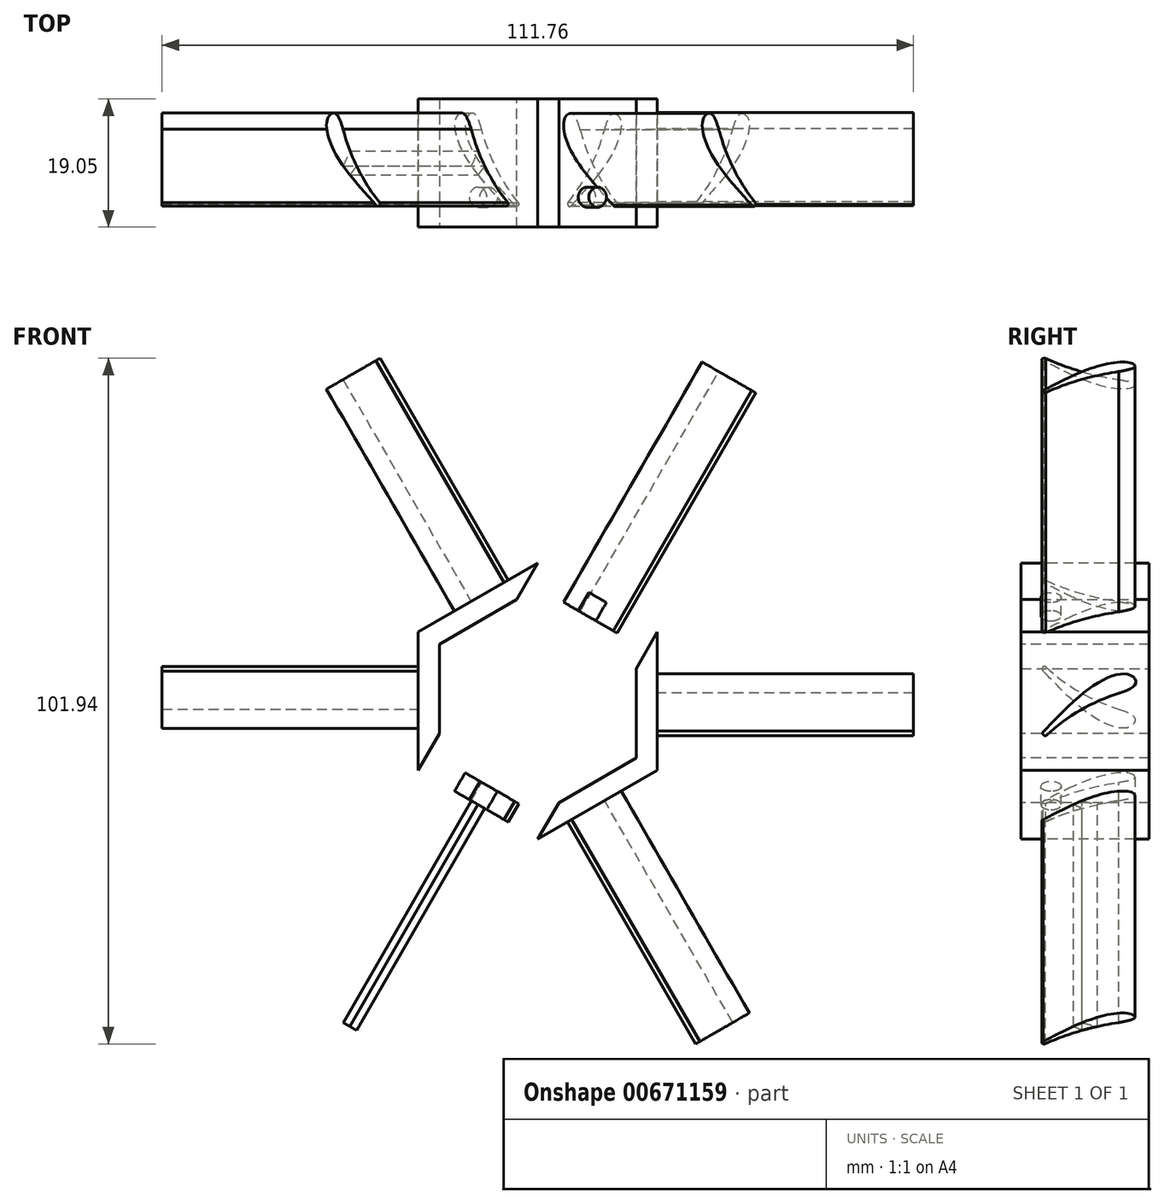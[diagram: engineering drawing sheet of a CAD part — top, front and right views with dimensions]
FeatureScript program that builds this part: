
annotation { "Feature Type Name" : "Feature", "Feature Type Description" : "" }
export const myFeature = defineFeature(function(context is Context, id is Id, definition is map)
    precondition{}
    {
        {
            var Q0;
            Q0=qCreatedBy(makeId("Front.planeOp"),FACE);
            var sketch = newSketch(context, id + "F0", { "sketchPlane" : qUnion([Q0])});
            skCircle(sketch, "E0.cCircle", {"center": v(0, 0) * mm, "radius": 17.78 * mm, "construction": true});
            skLineSegment(sketch, "E0.0", {"start": v(17.78, 10.27) * mm, "end": v(17.78, -10.27) * mm});
            skLineSegment(sketch, "E0.1", {"start": v(17.78, -10.27) * mm, "end": v(0, -20.53) * mm});
            skLineSegment(sketch, "E0.2", {"start": v(0, -20.53) * mm, "end": v(-17.78, -10.27) * mm});
            skLineSegment(sketch, "E0.3", {"start": v(-17.78, -10.27) * mm, "end": v(-17.78, 10.27) * mm});
            skLineSegment(sketch, "E0.4", {"start": v(-17.78, 10.27) * mm, "end": v(0, 20.53) * mm});
            skLineSegment(sketch, "E0.5", {"start": v(0, 20.53) * mm, "end": v(17.78, 10.27) * mm});
            skPoint(sketch, "E0.0.midPoint", {"position": v(17.78, 0) * mm});
            skSolve(sketch);
        }
        {
            var Q0;
            Q0=makeQuery(id+"F0.imprint","IMPRINT",FACE,{"disambiguationData":[TD([[makeQuery(id+"F0.imprint","IMPRINT",EDGE,{"derivedFrom":sQuery(id+"F0.wireOp",EDGE,"E0.0")}),-1.0]])]});
            extrude(context, id + "F1", {"entities" : qUnion([Q0]), "depth" : 19.05 * mm, "offsetDistance" : 25.4 * mm});
        }
        {
            var Q0;
            Q0=makeQuery(id+"F1.opExtrude","SWEPT_FACE",FACE,{"disambiguationData":[OSD([sQuery(id+"F0.wireOp",EDGE,"E0.5")])]});
            var sketch = newSketch(context, id + "F2", { "sketchPlane" : qUnion([Q0])});
            skLineSegment(sketch, "E1", {"start": v(0, 0) * mm, "end": v(0, -19.05) * mm});
            skPoint(sketch, "E2", {"position": v(0, -9.53) * mm});
            skFitSpline(sketch, "E3", {"points": [v(-1.19, -14.5) * mm, v(-2.57, -16.9) * mm, v(-3.83, -16.16) * mm, v(-2.94, -11.66) * mm, v(4.47, -3.26) * mm], "startDerivative": vector(-5.87, -16.48) * mm, "endDerivative": vector(22.04, 21.13) * mm});
            skArc(sketch, "E4", {"start": v(5.1, -3.62) * mm, "mid": v(1.33, -8.7) * mm, "end": v(-1.19, -14.5) * mm});
            skArc(sketch, "E5", {"start": v(5.1, -3.62) * mm, "mid": v(4.97, -3.12) * mm, "end": v(4.47, -3.26) * mm});
            skLineSegment(sketch, "E6", {"start": v(0, 0) * mm, "end": v(0, -4.45) * mm});
            skCircle(sketch, "E7", {"center": v(0, -4.45) * mm, "radius": 1.5 * mm});
            skSolve(sketch);
        }
        {
            var Q0;
            Q0=makeQuery(id+"F1.opExtrude","SWEPT_FACE",FACE,{"disambiguationData":[OSD([sQuery(id+"F0.wireOp",EDGE,"E0.0")])]});
            var sketch = newSketch(context, id + "F3", { "sketchPlane" : qUnion([Q0])});
            skLineSegment(sketch, "E8", {"start": v(0, 0) * mm, "end": v(-19.05, 0) * mm});
            skLineSegment(sketch, "E9", {"start": v(0.25, 0) * mm, "end": v(-18.8, 0) * mm});
            skFitSpline(sketch, "E10", {"points": [v(-14.64, 1.2) * mm, v(-17.02, 2.57) * mm, v(-16.3, 3.84) * mm, v(-11.79, 2.95) * mm, v(-3.39, -4.47) * mm], "startDerivative": vector(-16.48, 5.87) * mm, "endDerivative": vector(21.13, -22.04) * mm});
            skArc(sketch, "E11", {"start": v(-3.75, -5.1) * mm, "mid": v(-8.83, -1.33) * mm, "end": v(-14.64, 1.2) * mm});
            skArc(sketch, "E12", {"start": v(-3.75, -5.1) * mm, "mid": v(-3.25, -4.97) * mm, "end": v(-3.39, -4.47) * mm});
            skLineSegment(sketch, "E13", {"start": v(0, 0) * mm, "end": v(-4.44, 0) * mm});
            skCircle(sketch, "E14", {"center": v(-4.44, 0) * mm, "radius": 1.5 * mm});
            skSolve(sketch);
        }
        {
            var Q0;
            Q0=makeQuery(id+"F1.opExtrude","SWEPT_FACE",FACE,{"disambiguationData":[OSD([sQuery(id+"F0.wireOp",EDGE,"E0.1")])]});
            var sketch = newSketch(context, id + "F4", { "sketchPlane" : qUnion([Q0])});
            skLineSegment(sketch, "E15", {"start": v(0, 0) * mm, "end": v(0, 19.05) * mm});
            skLineSegment(sketch, "E16", {"start": v(0, 0) * mm, "end": v(0, 19.04) * mm});
            skFitSpline(sketch, "E17", {"points": [v(1.2, 14.5) * mm, v(2.57, 16.88) * mm, v(3.84, 16.15) * mm, v(2.95, 11.65) * mm, v(-4.46, 3.25) * mm], "startDerivative": vector(5.87, 16.48) * mm, "endDerivative": vector(-22.04, -21.13) * mm});
            skArc(sketch, "E18", {"start": v(-5.1, 3.61) * mm, "mid": v(-1.33, 8.7) * mm, "end": v(1.2, 14.5) * mm});
            skArc(sketch, "E19", {"start": v(-5.1, 3.61) * mm, "mid": v(-4.97, 3.11) * mm, "end": v(-4.46, 3.25) * mm});
            skLineSegment(sketch, "E20", {"start": v(0, 0) * mm, "end": v(0, 4.44) * mm});
            skCircle(sketch, "E21", {"center": v(0, 4.44) * mm, "radius": 1.5 * mm});
            skSolve(sketch);
        }
        {
            var Q0;
            Q0=makeQuery(id+"F1.opExtrude","SWEPT_FACE",FACE,{"disambiguationData":[OSD([sQuery(id+"F0.wireOp",EDGE,"E0.2")])]});
            var sketch = newSketch(context, id + "F5", { "sketchPlane" : qUnion([Q0])});
            skLineSegment(sketch, "E22", {"start": v(0, 0) * mm, "end": v(0, 19.05) * mm});
            skLineSegment(sketch, "E23", {"start": v(0, 0.04) * mm, "end": v(0, 19.09) * mm});
            skFitSpline(sketch, "E24", {"points": [v(1.18, 14.54) * mm, v(2.56, 16.93) * mm, v(3.83, 16.2) * mm, v(2.94, 11.7) * mm, v(-4.47, 3.3) * mm], "startDerivative": vector(5.87, 16.48) * mm, "endDerivative": vector(-22.04, -21.13) * mm});
            skArc(sketch, "E25", {"start": v(-5.11, 3.66) * mm, "mid": v(-1.34, 8.74) * mm, "end": v(1.18, 14.54) * mm});
            skArc(sketch, "E26", {"start": v(-5.11, 3.66) * mm, "mid": v(-4.98, 3.16) * mm, "end": v(-4.47, 3.3) * mm});
            skSolve(sketch);
        }
        {
            var Q0;
            Q0=makeQuery(id+"F1.opExtrude","SWEPT_FACE",FACE,{"disambiguationData":[OSD([sQuery(id+"F0.wireOp",EDGE,"E0.3")])]});
            var sketch = newSketch(context, id + "F6", { "sketchPlane" : qUnion([Q0])});
            skLineSegment(sketch, "E27", {"start": v(0, 0) * mm, "end": v(19.05, 0) * mm});
            skLineSegment(sketch, "E28", {"start": v(0.03, 0) * mm, "end": v(19.08, 0) * mm});
            skFitSpline(sketch, "E29", {"points": [v(14.53, -1.19) * mm, v(16.92, -2.57) * mm, v(16.19, -3.83) * mm, v(11.68, -2.94) * mm, v(3.28, 4.47) * mm], "startDerivative": vector(16.48, -5.87) * mm, "endDerivative": vector(-21.13, 22.04) * mm});
            skArc(sketch, "E30", {"start": v(3.65, 5.1) * mm, "mid": v(8.73, 1.33) * mm, "end": v(14.53, -1.19) * mm});
            skArc(sketch, "E31", {"start": v(3.65, 5.1) * mm, "mid": v(3.15, 4.97) * mm, "end": v(3.28, 4.47) * mm});
            skSolve(sketch);
        }
        {
            var Q0;
            Q0=makeQuery(id+"F1.opExtrude","SWEPT_FACE",FACE,{"disambiguationData":[OSD([sQuery(id+"F0.wireOp",EDGE,"E0.4")])]});
            var sketch = newSketch(context, id + "F7", { "sketchPlane" : qUnion([Q0])});
            skLineSegment(sketch, "E32", {"start": v(0, 0) * mm, "end": v(0, -19.05) * mm});
            skLineSegment(sketch, "E33", {"start": v(0, -0.02) * mm, "end": v(0, -19.07) * mm});
            skFitSpline(sketch, "E34", {"points": [v(-1.19, -14.52) * mm, v(-2.57, -16.91) * mm, v(-3.83, -16.18) * mm, v(-2.94, -11.68) * mm, v(4.47, -3.28) * mm], "startDerivative": vector(-5.87, -16.48) * mm, "endDerivative": vector(22.04, 21.13) * mm});
            skArc(sketch, "E35", {"start": v(5.1, -3.64) * mm, "mid": v(1.33, -8.72) * mm, "end": v(-1.19, -14.52) * mm});
            skArc(sketch, "E36", {"start": v(5.1, -3.64) * mm, "mid": v(4.97, -3.14) * mm, "end": v(4.47, -3.28) * mm});
            skSolve(sketch);
        }
        {
            var Q0;
            {var subQ0=sQuery(id+"F7.wireOp",EDGE,"E34");var subQ1=sQuery(id+"F7.wireOp",EDGE,"E32");var subQ2=makeQuery(id+"F7.imprint","INTERSECT",VERTEX,{"derivedFrom":[subQ1,subQ0]});Q0=makeQuery(id+"F7.imprint","IMPRINT",FACE,{"disambiguationData":[TD([[makeQuery(id+"F7.imprint","IMPRINT",EDGE,{"disambiguationData":[TD([[subQ2,-1.0]])],"derivedFrom":subQ1}),-1.0]])]});}
            var Q1;
            {var subQ5=sQuery(id+"F7.wireOp",EDGE,"E36");Q1=makeQuery(id+"F7.imprint","IMPRINT",FACE,{"disambiguationData":[TD([[makeQuery(id+"F7.imprint","IMPRINT",EDGE,{"derivedFrom":subQ5}),1.0]])]});}
            extrude(context, id + "F8", {"entities" : qUnion([Q0, Q1]), "operationType" : NewBodyOperationType.ADD, "depth" : 38.1 * mm, "offsetDistance" : 25.4 * mm});
        }
        {
            var Q0;
            {var subQ0=sQuery(id+"F2.wireOp",EDGE,"E3");var subQ1=sQuery(id+"F2.wireOp",EDGE,"E1");var subQ2=makeQuery(id+"F2.imprint","INTERSECT",VERTEX,{"derivedFrom":[subQ1,subQ0]});Q0=makeQuery(id+"F2.imprint","IMPRINT",FACE,{"disambiguationData":[TD([[makeQuery(id+"F2.imprint","IMPRINT",EDGE,{"disambiguationData":[TD([[subQ2,-1.0]])],"derivedFrom":subQ1}),-1.0]])]});}
            var Q1;
            {var subQ5=sQuery(id+"F2.wireOp",EDGE,"E5");Q1=makeQuery(id+"F2.imprint","IMPRINT",FACE,{"disambiguationData":[TD([[makeQuery(id+"F2.imprint","IMPRINT",EDGE,{"derivedFrom":subQ5}),1.0]])]});}
            extrude(context, id + "F9", {"entities" : qUnion([Q0, Q1]), "operationType" : NewBodyOperationType.ADD, "depth" : 38.1 * mm, "offsetDistance" : 25.4 * mm});
        }
        {
            var Q0;
            {var subQ0=sQuery(id+"F3.wireOp",EDGE,"E10");var subQ1=sQuery(id+"F3.wireOp",EDGE,"E9");var subQ2=makeQuery(id+"F3.imprint","INTERSECT",VERTEX,{"derivedFrom":[subQ1,subQ0]});Q0=makeQuery(id+"F3.imprint","IMPRINT",FACE,{"disambiguationData":[TD([[makeQuery(id+"F3.imprint","IMPRINT",EDGE,{"disambiguationData":[TD([[subQ2,-1.0]])],"derivedFrom":subQ1}),-1.0]])]});}
            var Q1;
            {var subQ5=sQuery(id+"F3.wireOp",EDGE,"E12");Q1=makeQuery(id+"F3.imprint","IMPRINT",FACE,{"disambiguationData":[TD([[makeQuery(id+"F3.imprint","IMPRINT",EDGE,{"derivedFrom":subQ5}),1.0]])]});}
            extrude(context, id + "F10", {"entities" : qUnion([Q0, Q1]), "operationType" : NewBodyOperationType.ADD, "depth" : 38.1 * mm, "offsetDistance" : 25.4 * mm});
        }
        {
            var Q0;
            {var subQ0=sQuery(id+"F4.wireOp",EDGE,"E18");var subQ1=sQuery(id+"F4.wireOp",EDGE,"E16");var subQ2=makeQuery(id+"F4.imprint","INTERSECT",VERTEX,{"derivedFrom":[subQ1,subQ0]});Q0=makeQuery(id+"F4.imprint","IMPRINT",FACE,{"disambiguationData":[TD([[makeQuery(id+"F4.imprint","IMPRINT",EDGE,{"disambiguationData":[TD([[subQ2,1.0]])],"derivedFrom":subQ1}),-1.0]])]});}
            var Q1;
            {var subQ5=sQuery(id+"F4.wireOp",EDGE,"E19");Q1=makeQuery(id+"F4.imprint","IMPRINT",FACE,{"disambiguationData":[TD([[makeQuery(id+"F4.imprint","IMPRINT",EDGE,{"derivedFrom":subQ5}),1.0]])]});}
            extrude(context, id + "F11", {"entities" : qUnion([Q0, Q1]), "operationType" : NewBodyOperationType.ADD, "depth" : 38.1 * mm, "offsetDistance" : 25.4 * mm});
        }
        {
            var Q0;
            {var subQ0=sQuery(id+"F5.wireOp",EDGE,"E24");var subQ1=sQuery(id+"F5.wireOp",EDGE,"E22");var subQ2=makeQuery(id+"F5.imprint","INTERSECT",VERTEX,{"derivedFrom":[subQ1,subQ0]});Q0=makeQuery(id+"F5.imprint","IMPRINT",FACE,{"disambiguationData":[TD([[makeQuery(id+"F5.imprint","IMPRINT",EDGE,{"disambiguationData":[TD([[subQ2,-1.0]])],"derivedFrom":subQ1}),-1.0]])]});}
            var Q1;
            {var subQ5=sQuery(id+"F5.wireOp",EDGE,"E26");Q1=makeQuery(id+"F5.imprint","IMPRINT",FACE,{"disambiguationData":[TD([[makeQuery(id+"F5.imprint","IMPRINT",EDGE,{"derivedFrom":subQ5}),1.0]])]});}
            extrude(context, id + "F12", {"entities" : qUnion([Q0, Q1]), "operationType" : NewBodyOperationType.ADD, "depth" : 38.1 * mm, "offsetDistance" : 25.4 * mm});
        }
        {
            var Q0;
            {var subQ0=sQuery(id+"F6.wireOp",EDGE,"E29");var subQ1=sQuery(id+"F6.wireOp",EDGE,"E27");var subQ2=makeQuery(id+"F6.imprint","INTERSECT",VERTEX,{"derivedFrom":[subQ1,subQ0]});Q0=makeQuery(id+"F6.imprint","IMPRINT",FACE,{"disambiguationData":[TD([[makeQuery(id+"F6.imprint","IMPRINT",EDGE,{"disambiguationData":[TD([[subQ2,-1.0]])],"derivedFrom":subQ1}),-1.0]])]});}
            var Q1;
            {var subQ5=sQuery(id+"F6.wireOp",EDGE,"E31");Q1=makeQuery(id+"F6.imprint","IMPRINT",FACE,{"disambiguationData":[TD([[makeQuery(id+"F6.imprint","IMPRINT",EDGE,{"derivedFrom":subQ5}),1.0]])]});}
            extrude(context, id + "F13", {"entities" : qUnion([Q0, Q1]), "operationType" : NewBodyOperationType.ADD, "depth" : 38.1 * mm, "offsetDistance" : 25.4 * mm});
        }
        {
            var Q0;
            Q0=makeQuery(id+"F1.opExtrude","CAP_FACE",FACE,{"disambiguationData":[OSD([sQuery(id+"F0.wireOp",EDGE,"E0.0"),sQuery(id+"F0.wireOp",EDGE,"E0.1"),sQuery(id+"F0.wireOp",EDGE,"E0.2"),sQuery(id+"F0.wireOp",EDGE,"E0.3"),sQuery(id+"F0.wireOp",EDGE,"E0.4"),sQuery(id+"F0.wireOp",EDGE,"E0.5")])],"isStart":false});
            cPlane(context, id + "F14", {"entities" : qUnion([Q0]), "cplaneType" : CPlaneType.OFFSET, "offset" : 6.35 * mm, "width" : 152.4 * mm, "height" : 152.4 * mm});
        }
        {
            var Q0;
            Q0=makeQuery(id+"F1.opExtrude","CAP_FACE",FACE,{"disambiguationData":[OSD([sQuery(id+"F0.wireOp",EDGE,"E0.0"),sQuery(id+"F0.wireOp",EDGE,"E0.1"),sQuery(id+"F0.wireOp",EDGE,"E0.2"),sQuery(id+"F0.wireOp",EDGE,"E0.3"),sQuery(id+"F0.wireOp",EDGE,"E0.4"),sQuery(id+"F0.wireOp",EDGE,"E0.5")])],"isStart":true});
            var sketch = newSketch(context, id + "F15", { "sketchPlane" : qUnion([Q0])});
            skCircle(sketch, "E37.cCircle", {"center": v(0, 0) * mm, "radius": 14.64 * mm, "construction": true});
            skLineSegment(sketch, "E37.0", {"start": v(0, -16.9) * mm, "end": v(-14.64, -8.45) * mm});
            skLineSegment(sketch, "E37.1", {"start": v(-14.64, -8.45) * mm, "end": v(-14.64, 8.45) * mm});
            skLineSegment(sketch, "E37.2", {"start": v(-14.64, 8.45) * mm, "end": v(0, 16.9) * mm});
            skLineSegment(sketch, "E37.3", {"start": v(0, 16.9) * mm, "end": v(14.64, 8.45) * mm});
            skLineSegment(sketch, "E37.4", {"start": v(14.64, 8.45) * mm, "end": v(14.64, -8.45) * mm});
            skLineSegment(sketch, "E37.5", {"start": v(14.64, -8.45) * mm, "end": v(0, -16.9) * mm});
            skPoint(sketch, "E37.0.midPoint", {"position": v(-7.32, -12.68) * mm});
            skSolve(sketch);
        }
        {
            var Q0;
            Q0=makeQuery(id+"F15.imprint","IMPRINT",FACE,{"disambiguationData":[TD([[makeQuery(id+"F15.imprint","IMPRINT",EDGE,{"derivedFrom":sQuery(id+"F15.wireOp",EDGE,"E37.0")}),-1.0]])]});
            extrude(context, id + "F16", {"entities" : qUnion([Q0]), "operationType" : NewBodyOperationType.REMOVE, "endBound" : BoundingType.THROUGH_ALL, "oppositeDirection" : true, "depth" : 25.4 * mm, "offsetDistance" : 25.4 * mm});
        }
        {
            var Q0;
            {var subQ0=sQuery(id+"F2.wireOp",EDGE,"E6");var subQ1=sQuery(id+"F2.wireOp",EDGE,"E1");var subQ2=makeQuery(id+"F2.imprint","INTERSECT",VERTEX,{"derivedFrom":[subQ1,subQ0]});Q0=makeQuery(id+"F2.imprint","IMPRINT",FACE,{"disambiguationData":[TD([[makeQuery(id+"F2.imprint","IMPRINT",EDGE,{"disambiguationData":[TD([[subQ2,-1.0]])],"derivedFrom":subQ1}),1.0]])]});}
            var Q1;
            {var subQ0=sQuery(id+"F2.wireOp",EDGE,"E6");var subQ1=sQuery(id+"F2.wireOp",EDGE,"E1");var subQ2=makeQuery(id+"F2.imprint","INTERSECT",VERTEX,{"derivedFrom":[subQ1,subQ0]});Q1=makeQuery(id+"F2.imprint","IMPRINT",FACE,{"disambiguationData":[TD([[makeQuery(id+"F2.imprint","IMPRINT",EDGE,{"disambiguationData":[TD([[subQ2,-1.0]])],"derivedFrom":subQ1}),-1.0]])]});}
            extrude(context, id + "F17", {"entities" : qUnion([Q0, Q1]), "operationType" : NewBodyOperationType.REMOVE, "endBound" : BoundingType.THROUGH_ALL, "oppositeDirection" : true, "depth" : 25.4 * mm, "offsetDistance" : 25.4 * mm});
        }
        {
            var Q0;
            Q0=makeQuery(id+"F1.opExtrude","SWEPT_BODY",BODY,{"disambiguationData":[OSD([sQuery(id+"F0.wireOp",EDGE,"E0.0"),sQuery(id+"F0.wireOp",EDGE,"E0.1"),sQuery(id+"F0.wireOp",EDGE,"E0.2"),sQuery(id+"F0.wireOp",EDGE,"E0.3"),sQuery(id+"F0.wireOp",EDGE,"E0.4"),sQuery(id+"F0.wireOp",EDGE,"E0.5")])]});
            var Q1;
            Q1=qCreatedBy(id+"F14.planeOp",FACE);
            mirror(context, id + "F18", {"entities" : qUnion([Q0]), "mirrorPlane" : qUnion([Q1])});
        }
        {
            var Q0;
            Q0=makeQuery(id+"F1.opExtrude","SWEPT_BODY",BODY,{"disambiguationData":[OSD([sQuery(id+"F0.wireOp",EDGE,"E0.0"),sQuery(id+"F0.wireOp",EDGE,"E0.1"),sQuery(id+"F0.wireOp",EDGE,"E0.2"),sQuery(id+"F0.wireOp",EDGE,"E0.3"),sQuery(id+"F0.wireOp",EDGE,"E0.4"),sQuery(id+"F0.wireOp",EDGE,"E0.5")])]});
            deleteBodies(context, id + "F19", {"entities" : qUnion([Q0])});
        }
        {
            var Q0;
            {var subQ0=sQuery(id+"F4.wireOp",EDGE,"E20");var subQ1=sQuery(id+"F4.wireOp",EDGE,"E16");var subQ2=makeQuery(id+"F4.imprint","INTERSECT",VERTEX,{"derivedFrom":[subQ1,subQ0]});Q0=makeQuery(id+"F4.imprint","IMPRINT",FACE,{"disambiguationData":[TD([[makeQuery(id+"F4.imprint","IMPRINT",EDGE,{"disambiguationData":[TD([[subQ2,-1.0]])],"derivedFrom":subQ1}),-1.0]])]});}
            var Q1;
            {var subQ0=sQuery(id+"F4.wireOp",EDGE,"E21");var subQ1=sQuery(id+"F4.wireOp",EDGE,"E15");var subQ2=makeQuery(id+"F4.imprint","INTERSECT",VERTEX,{"disambiguationData":[OD(0.0)],"derivedFrom":[subQ1,subQ0]});Q1=makeQuery(id+"F4.imprint","IMPRINT",FACE,{"disambiguationData":[TD([[makeQuery(id+"F4.imprint","IMPRINT",EDGE,{"disambiguationData":[TD([[subQ2,-1.0]])],"derivedFrom":subQ1}),1.0]])]});}
            extrude(context, id + "F20", {"entities" : qUnion([Q0, Q1]), "operationType" : NewBodyOperationType.REMOVE, "endBound" : BoundingType.THROUGH_ALL, "oppositeDirection" : true, "depth" : 25.4 * mm, "offsetDistance" : 25.4 * mm});
        }
        {
            var Q0;
            {var subQ0=sQuery(id+"F3.wireOp",EDGE,"E9");var subQ1=makeQuery(id+"F3.imprint","INTERSECT",VERTEX,{"derivedFrom":[subQ0,sQuery(id+"F3.wireOp",EDGE,"E13")]});Q0=makeQuery(id+"F3.imprint","IMPRINT",FACE,{"disambiguationData":[TD([[makeQuery(id+"F3.imprint","IMPRINT",EDGE,{"disambiguationData":[TD([[subQ1,1.0]])],"derivedFrom":subQ0}),-1.0]])]});}
            var Q1;
            {var subQ0=sQuery(id+"F3.wireOp",EDGE,"E14");var subQ1=sQuery(id+"F3.wireOp",EDGE,"E8");var subQ2=makeQuery(id+"F3.imprint","INTERSECT",VERTEX,{"disambiguationData":[OD(0.0)],"derivedFrom":[subQ1,subQ0]});Q1=makeQuery(id+"F3.imprint","IMPRINT",FACE,{"disambiguationData":[TD([[makeQuery(id+"F3.imprint","IMPRINT",EDGE,{"disambiguationData":[TD([[subQ2,-1.0]])],"derivedFrom":subQ1}),1.0]])]});}
            extrude(context, id + "F21", {"entities" : qUnion([Q0, Q1]), "operationType" : NewBodyOperationType.REMOVE, "endBound" : BoundingType.THROUGH_ALL, "oppositeDirection" : true, "depth" : 25.4 * mm, "offsetDistance" : 25.4 * mm});
        }
    });
